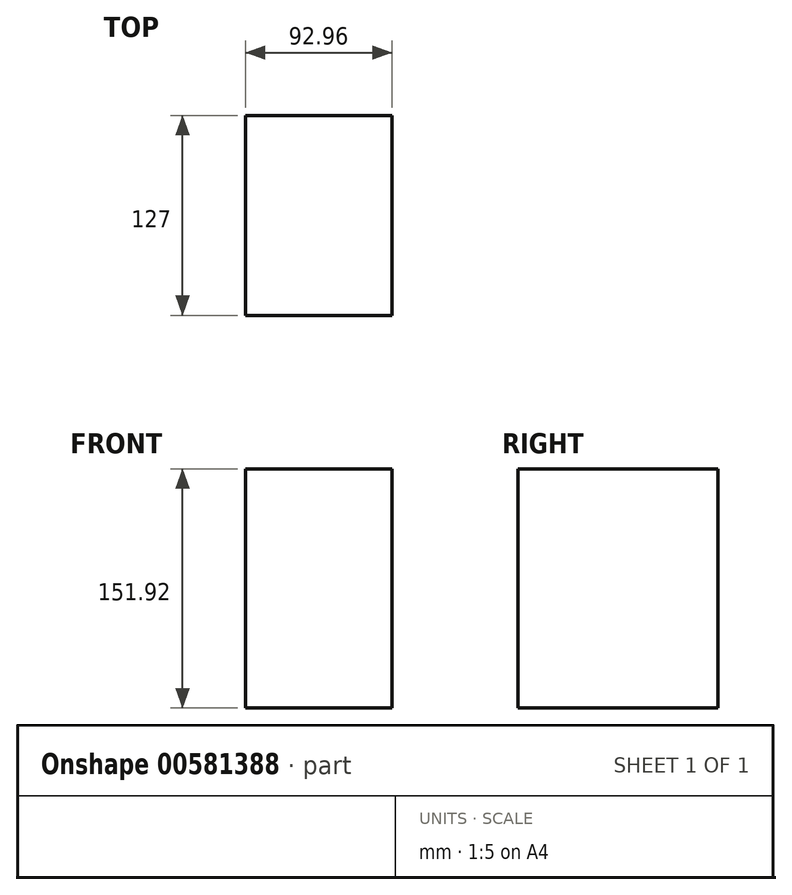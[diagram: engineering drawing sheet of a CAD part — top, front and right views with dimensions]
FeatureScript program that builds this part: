
annotation { "Feature Type Name" : "Feature", "Feature Type Description" : "" }
export const myFeature = defineFeature(function(context is Context, id is Id, definition is map)
    precondition{}
    {
        {
            var Q0;
            Q0=qCreatedBy(makeId("Front.planeOp"),FACE);
            var sketch = newSketch(context, id + "F0", { "sketchPlane" : qUnion([Q0])});
            skLineSegment(sketch, "E0.bottom", {"start": v(-49.73, 77.21) * mm, "end": v(43.23, 77.21) * mm});
            skLineSegment(sketch, "E0.top", {"start": v(-49.73, -74.71) * mm, "end": v(43.23, -74.71) * mm});
            skLineSegment(sketch, "E0.left", {"start": v(-49.73, 77.21) * mm, "end": v(-49.73, -74.71) * mm});
            skLineSegment(sketch, "E0.right", {"start": v(43.23, 77.21) * mm, "end": v(43.23, -74.71) * mm});
            skSolve(sketch);
        }
        {
            var Q0;
            Q0 = qSketchRegion(id + "F0", true);
            extrude(context, id + "F1", {"entities" : qUnion([Q0]), "depth" : 127 * mm, "offsetDistance" : 25.4 * mm});
        }
    });
